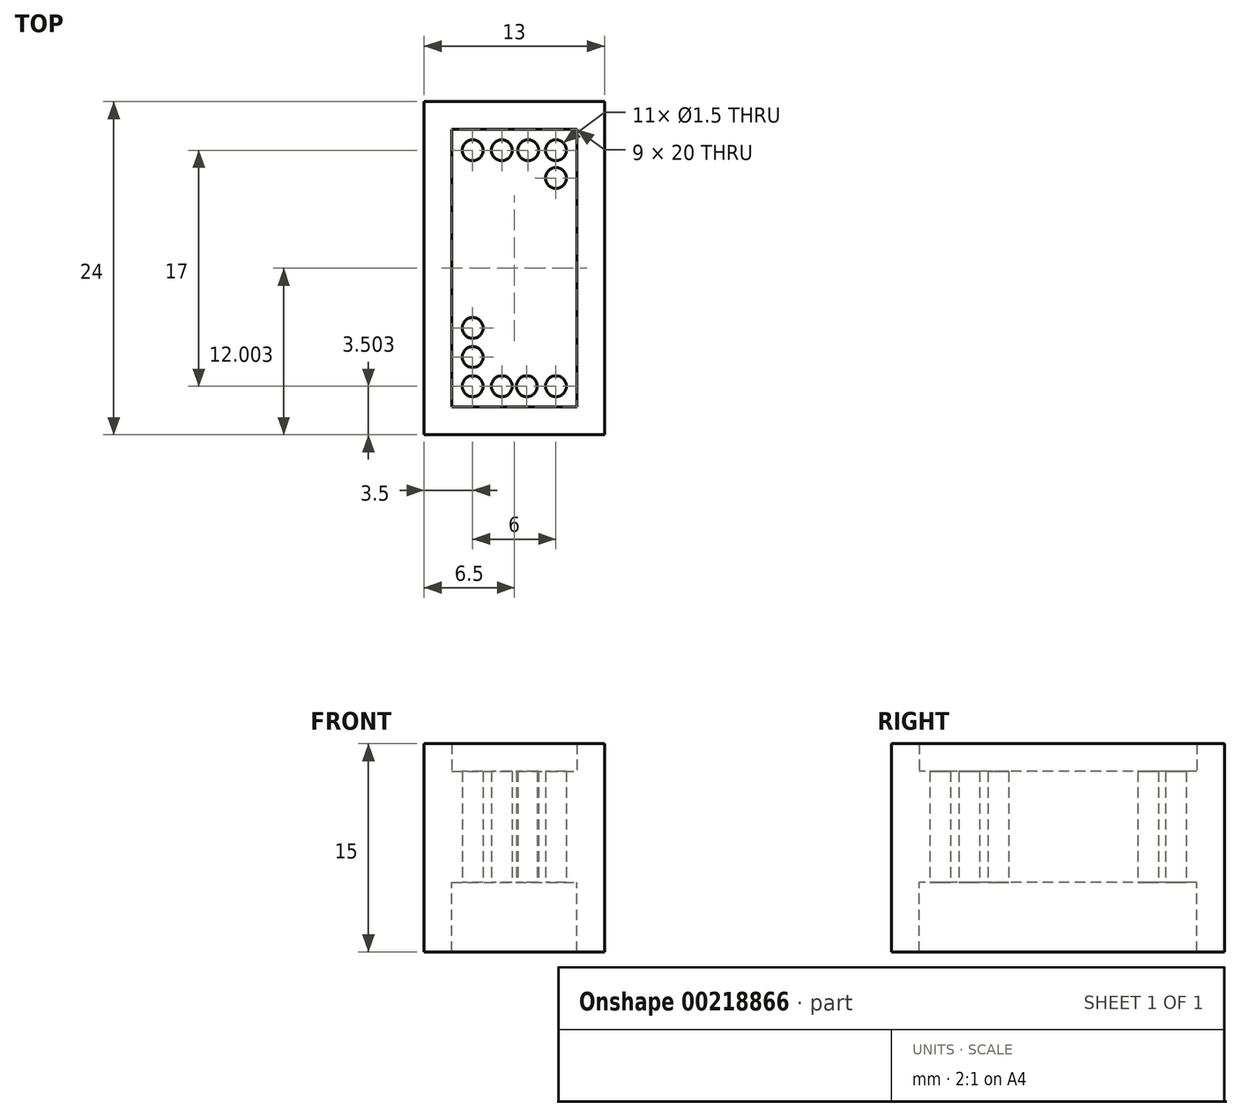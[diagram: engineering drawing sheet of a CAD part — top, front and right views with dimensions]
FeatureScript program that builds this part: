
annotation { "Feature Type Name" : "Feature", "Feature Type Description" : "" }
export const myFeature = defineFeature(function(context is Context, id is Id, definition is map)
    precondition{}
    {
        {
            var Q0;
            Q0=qCreatedBy(makeId("Top.planeOp"),FACE);
            var sketch = newSketch(context, id + "F0", { "sketchPlane" : qUnion([Q0])});
            skCircle(sketch, "E0", {"center": v(5.42, -13.1) * mm, "radius": 0.75 * mm});
            skCircle(sketch, "E1", {"center": v(7.52, -13.1) * mm, "radius": 0.75 * mm});
            skCircle(sketch, "E2", {"center": v(9.32, -13.1) * mm, "radius": 0.75 * mm});
            skCircle(sketch, "E3", {"center": v(11.42, -13.1) * mm, "radius": 0.75 * mm});
            skCircle(sketch, "E4", {"center": v(5.42, -11) * mm, "radius": 0.75 * mm});
            skCircle(sketch, "E5", {"center": v(5.42, -8.9) * mm, "radius": 0.75 * mm});
            skCircle(sketch, "E6", {"center": v(5.42, 3.9) * mm, "radius": 0.75 * mm});
            skCircle(sketch, "E7", {"center": v(7.52, 3.9) * mm, "radius": 0.75 * mm});
            skCircle(sketch, "E8", {"center": v(9.42, 3.9) * mm, "radius": 0.75 * mm});
            skCircle(sketch, "E9", {"center": v(11.42, 3.9) * mm, "radius": 0.75 * mm});
            skCircle(sketch, "E10", {"center": v(11.42, 1.9) * mm, "radius": 0.75 * mm});
            skLineSegment(sketch, "E11.bottom", {"start": v(4.42, -14.1) * mm, "end": v(12.42, -14.1) * mm, "construction": true});
            skLineSegment(sketch, "E11.top", {"start": v(4.42, 4.9) * mm, "end": v(12.42, 4.9) * mm, "construction": true});
            skLineSegment(sketch, "E11.left", {"start": v(4.42, -14.1) * mm, "end": v(4.42, 4.9) * mm, "construction": true});
            skLineSegment(sketch, "E11.right", {"start": v(12.42, -14.1) * mm, "end": v(12.42, 4.9) * mm, "construction": true});
            skLineSegment(sketch, "E12.bottom", {"start": v(3.92, 5.4) * mm, "end": v(12.92, 5.4) * mm});
            skLineSegment(sketch, "E12.top", {"start": v(3.92, -14.6) * mm, "end": v(12.92, -14.6) * mm});
            skLineSegment(sketch, "E12.left", {"start": v(3.92, 5.4) * mm, "end": v(3.92, -14.6) * mm});
            skLineSegment(sketch, "E12.right", {"start": v(12.92, 5.4) * mm, "end": v(12.92, -14.6) * mm});
            skLineSegment(sketch, "E13.bottom", {"start": v(1.92, 7.4) * mm, "end": v(14.92, 7.4) * mm});
            skLineSegment(sketch, "E13.top", {"start": v(1.92, -16.6) * mm, "end": v(14.92, -16.6) * mm});
            skLineSegment(sketch, "E13.left", {"start": v(1.92, 7.4) * mm, "end": v(1.92, -16.6) * mm});
            skLineSegment(sketch, "E13.right", {"start": v(14.92, 7.4) * mm, "end": v(14.92, -16.6) * mm});
            skSolve(sketch);
        }
        {
            var Q0;
            Q0=makeQuery(id+"F0.imprint","IMPRINT",FACE,{"disambiguationData":[TD([[makeQuery(id+"F0.imprint","IMPRINT",EDGE,{"derivedFrom":sQuery(id+"F0.wireOp",EDGE,"E12.bottom")}),1.0]])]});
            var Q1;
            {var subQ0=sQuery(id+"F0.wireOp",EDGE,"E12.top");Q1=makeQuery(id+"F0.imprint","IMPRINT",FACE,{"disambiguationData":[TD([[makeQuery(id+"F0.imprint","IMPRINT",EDGE,{"derivedFrom":subQ0}),-1.0]])]});}
            extrude(context, id + "F1", {"entities" : qUnion([Q0, Q1]), "depth" : 10 * mm});
        }
        {
            var Q0;
            Q0=makeQuery(id+"F0.imprint","IMPRINT",FACE,{"disambiguationData":[TD([[makeQuery(id+"F0.imprint","IMPRINT",EDGE,{"derivedFrom":sQuery(id+"F0.wireOp",EDGE,"E0")}),-1.0]])]});
            var Q1;
            Q1=makeQuery(id+"F0.imprint","IMPRINT",FACE,{"disambiguationData":[TD([[makeQuery(id+"F0.imprint","IMPRINT",EDGE,{"derivedFrom":sQuery(id+"F0.wireOp",EDGE,"E12.bottom")}),1.0]])]});
            var Q2;
            {var subQ0=sQuery(id+"F0.wireOp",EDGE,"E12.top");Q2=makeQuery(id+"F0.imprint","IMPRINT",FACE,{"disambiguationData":[TD([[makeQuery(id+"F0.imprint","IMPRINT",EDGE,{"derivedFrom":subQ0}),-1.0]])]});}
            extrude(context, id + "F2", {"entities" : qUnion([Q0, Q1, Q2]), "operationType" : NewBodyOperationType.ADD, "depth" : 8 * mm});
        }
        {
            var Q0;
            Q0=makeQuery(id+"F0.imprint","IMPRINT",FACE,{"disambiguationData":[TD([[makeQuery(id+"F0.imprint","IMPRINT",EDGE,{"derivedFrom":sQuery(id+"F0.wireOp",EDGE,"E12.bottom")}),1.0]])]});
            var Q1;
            {var subQ0=sQuery(id+"F0.wireOp",EDGE,"E12.top");Q1=makeQuery(id+"F0.imprint","IMPRINT",FACE,{"disambiguationData":[TD([[makeQuery(id+"F0.imprint","IMPRINT",EDGE,{"derivedFrom":subQ0}),-1.0]])]});}
            extrude(context, id + "F3", {"entities" : qUnion([Q0, Q1]), "operationType" : NewBodyOperationType.ADD, "oppositeDirection" : true, "depth" : 5 * mm});
        }
    });
